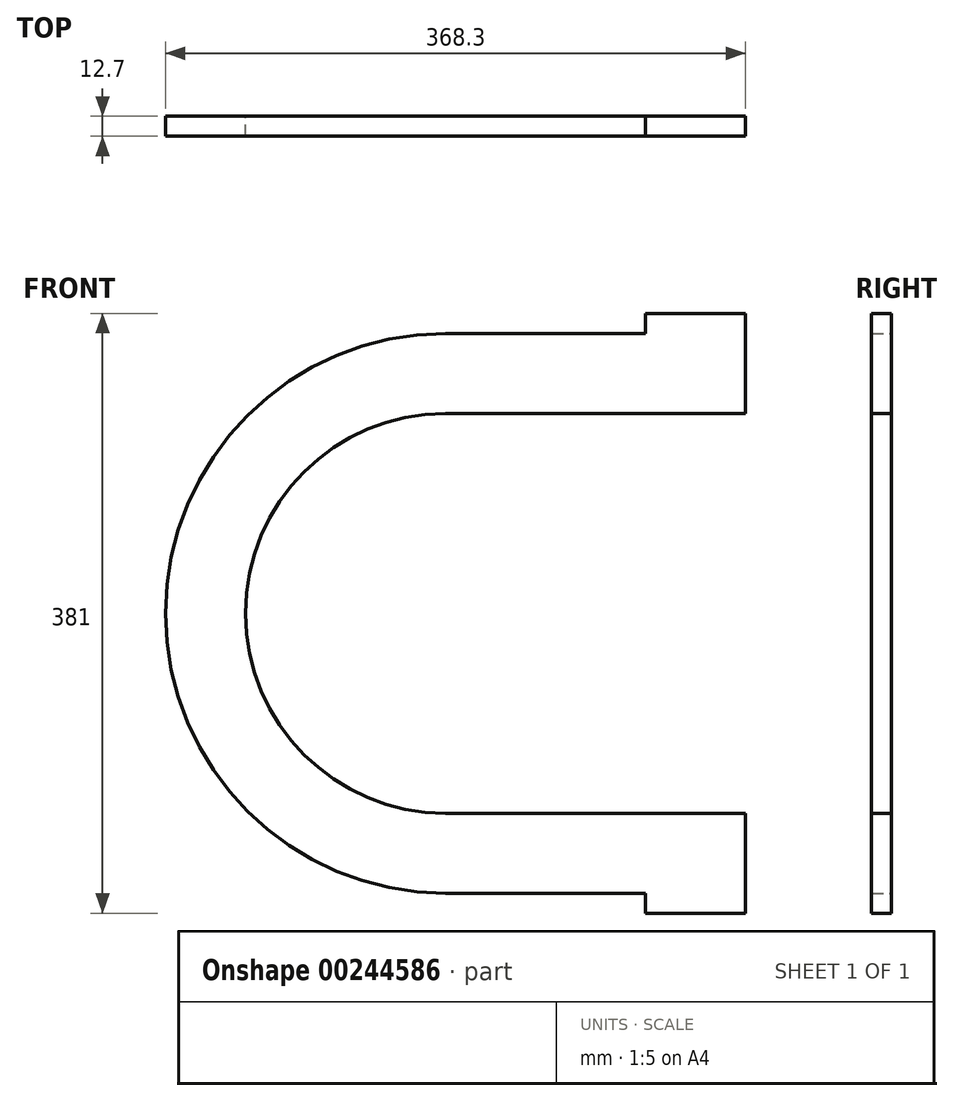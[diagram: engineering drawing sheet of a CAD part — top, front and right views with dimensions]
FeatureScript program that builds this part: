
annotation { "Feature Type Name" : "Feature", "Feature Type Description" : "" }
export const myFeature = defineFeature(function(context is Context, id is Id, definition is map)
    precondition{}
    {
        {
            var Q0;
            Q0=qCreatedBy(makeId("Front.planeOp"),FACE);
            var sketch = newSketch(context, id + "F0", { "sketchPlane" : qUnion([Q0])});
            skLineSegment(sketch, "E0.bottom", {"start": v(127, -177.8) * mm, "end": v(0, -177.8) * mm});
            skLineSegment(sketch, "E0.top", {"start": v(127, 177.8) * mm, "end": v(0, 177.8) * mm});
            skLineSegment(sketch, "E0.left", {"start": v(190.5, -177.8) * mm, "end": v(190.5, -127) * mm});
            skPoint(sketch, "E0.middle", {"position": v(0, 0) * mm});
            skArc(sketch, "E1", {"start": v(0, 127) * mm, "mid": v(-127, 0) * mm, "end": v(0, -127) * mm});
            skLineSegment(sketch, "E2", {"start": v(0, 127) * mm, "end": v(190.5, 127) * mm});
            skLineSegment(sketch, "E3", {"start": v(0, -127) * mm, "end": v(190.5, -127) * mm});
            skArc(sketch, "E4", {"start": v(0, 177.8) * mm, "mid": v(-177.8, 0) * mm, "end": v(0, -177.8) * mm});
            skLineSegment(sketch, "E5.trimOffspring", {"start": v(190.5, 127) * mm, "end": v(190.5, 177.8) * mm});
            skPoint(sketch, "E6.orphan", {"position": v(-190.5, -177.8) * mm});
            skPoint(sketch, "E7.orphan", {"position": v(-190.5, 177.8) * mm});
            skLineSegment(sketch, "E8.bottom", {"start": v(127, -127) * mm, "end": v(190.5, -127) * mm});
            skLineSegment(sketch, "E8.top", {"start": v(127, -190.5) * mm, "end": v(190.5, -190.5) * mm});
            skLineSegment(sketch, "E8.left", {"start": v(127, -177.8) * mm, "end": v(127, -190.5) * mm});
            skLineSegment(sketch, "E8.right", {"start": v(190.5, -127) * mm, "end": v(190.5, -190.5) * mm});
            skLineSegment(sketch, "E9.bottom", {"start": v(127, 127) * mm, "end": v(190.5, 127) * mm});
            skLineSegment(sketch, "E9.top", {"start": v(127, 190.5) * mm, "end": v(190.5, 190.5) * mm});
            skLineSegment(sketch, "E9.left", {"start": v(127, 177.8) * mm, "end": v(127, 190.5) * mm});
            skLineSegment(sketch, "E9.right", {"start": v(190.5, 127) * mm, "end": v(190.5, 190.5) * mm});
            skSolve(sketch);
        }
        {
            var Q0;
            Q0 = qSketchRegion(id + "F0", true);
            extrude(context, id + "F1", {"entities" : qUnion([Q0]), "depth" : 12.7 * mm});
        }
    });
